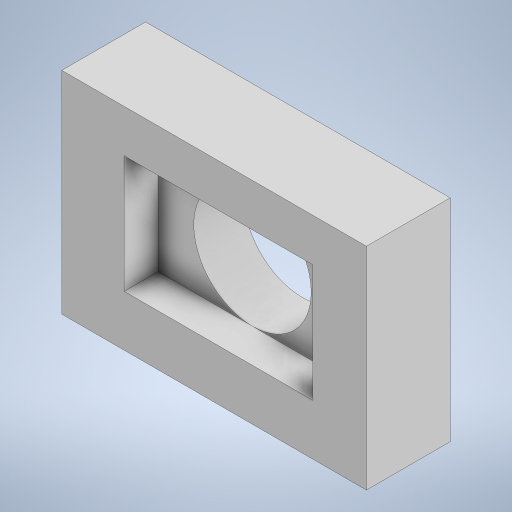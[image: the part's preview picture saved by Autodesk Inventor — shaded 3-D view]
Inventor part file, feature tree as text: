
AUTODESK INVENTOR PART (.ipt)
format: ipt  version: 2023 (Build 270158000, 158)  size: 631,296 bytes
history: native  units: in
note: dims shown in document units (in); Inventor stores cm internally (conversion verified against a paired STEP export)
features: extrude x18, sketch x16, fillet x2
ambient origin geometry x8: Origin, YZ Plane, XZ Plane, XY Plane, X Axis, Y Axis, Z Axis, Center Point
bodies: Solid1 (feature_tree)
feature tree (36):
  extrude  "Extrusion1"  Depth=4.5in
  extrude  "Extrusion2"  Depth=0.2in
  fillet  "Fillet1"  Radius=1.4in
  extrude  "Extrusion3"  Depth=0.25in
  extrude  "Extrusion4"  Depth=2.2875in
  extrude  "Extrusion5"  Depth=0.5437in
  sketch  "Sketch6"  dims[d13=0.75in d14=1.4in d15=0.0in]
  extrude  "Extrusion6"  Depth=1.4in TaperAngle=0.0deg
  extrude  "Extrusion9"  Depth=0.14in
  extrude  "Extrusion10"  Depth=0.275in
  extrude  "Extrusion11"  Depth=0.25in
  extrude  "Extrusion12"  Depth=0.15in
  extrude  "Extrusion13"  Depth=0.7in
  extrude  "Extrusion14"  Depth=0.1in
  extrude  "Extrusion15"  Depth=0.615in
  extrude  "Extrusion16"  Depth=1.1in
  fillet  "Fillet2"  Radius=0.21in
  extrude  "Extrusion17"  Depth=0.5575in
  extrude  "Extrusion18"  Depth=0.14in
  extrude  "Extrusion19"  Depth=0.14in
  extrude  "Extrusion20"  Depth=0.14in
  sketch  "Sketch1"  dims[d0=7.0in d1=4.5in]
  sketch  "Sketch2"  dims[d2=1.5in d3=0.0in d4=0.2in d5=1.4in d6=0.0in]
  sketch  "Sketch3"  dims[d7=0.125in d8=0.25in]
  sketch  "Sketch4"  dims[d9=0.25in d10=2.2875in]
  sketch  "Sketch5"  dims[d11=3.4125in d12=0.5437in]
  sketch  "Sketch8"  dims[d16=0.1in d17=0.14in]
  sketch  "Sketch9"  dims[d18=0.1in d19=0.275in]
  sketch  "Sketch10"  dims[d20=0.35in d21=0.25in]
  sketch  "Sketch11"  dims[d22=0.15in d23=0.15in]
  sketch  "Sketch12"  dims[d24=0.25in d25=0.7in]
  sketch  "Sketch13"  dims[d26=0.1in d27=0.1in]
  sketch  "Sketch14"  dims[d28=0.25in d29=0.615in]
  sketch  "Sketch15"  dims[d30=0.25in d31=1.1in d32=0.21in]
  sketch  "Sketch16"  dims[d33=0.3075in d34=0.5575in]
  sketch  "Sketch17"  dims[d35=1.65in d36=0.3075in d37=0.21in d38=0.5575in d39=2.1in d40=0.1in d41=0.1in d42=0.3in d43=0.1in d44=0.25in d45=0.615in d46=2.4in d47=0.11in d48=2.51in d49=0.5575in d50=0.1in d51=0.615in d52=0.175in d53=0.175in d54=0.1in d55=0.1in d56=0.25in d57=3.15in d58=0.1in d59=0.515in d60=0.05in d61=0.0in d62=0.1562in d63=0.1562in d64=0.2188in d65=0.2188in d66=0.2188in d67=0.2188in d68=0.2188in d69=0.2188in d70=0.625in d71=0.625in d72=0.625in d73=0.625in d74=0.8906in d76=2.25in d77=0.3in d78=0.3in d79=0.3in d80=0.3in d81=0.3in d82=0.625in d83=0.625in d84=0.625in d85=0.625in d86=1.0in d87=3.1in d88=3.1in d89=3.1in d90=3.1in d91=3.1in d92=1.0in d93=0.0in d97=0.4in d98=0.4in d99=0.4in d100=0.4in d101=0.4in d102=0.05in d103=0.0in d119=0.075in d120=0.075in d121=0.075in d122=0.075in d123=0.075in d124=0.0688in d125=0.0in d126=0.25in d127=0.275in d128=0.25in d129=0.25in d130=0.25in d131=2.1in d132=0.125in d133=0.0625in d134=0.05in d135=0.0in d136=0.6in d137=3.35in d139=0.3in d140=0.3155in d141=0.3157in d142=0.0375in d143=0.0in d144=2.0in d145=0.8125in d146=0.0825in d147=0.35in d148=0.15in d149=0.1in d150=0.7in d151=0.2in d152=0.0in d153=0.075in d154=0.125in d155=0.0in d156=0.28in d157=2.5in d158=0.49in d159=0.25in d160=0.0in d161=0.45in d162=0.081in d163=0.0in d164=0.45in d166=0.2in d167=0.2in d168=0.2in d169=0.075in d170=0.075in d171=0.075in d172=0.075in d173=0.2in d174=0.2in d175=0.2in d176=0.2in d177=0.075in d178=0.0in d179=0.125in d180=0.0375in d181=0.0375in d182=2.0in d183=0.5in d184=0.0in d185=0.0in d187=2.8in d188=5.0in d189=0.0in d190=5.0in d191=0.0in d192=1.0in d193=0.0in d194=0.28in d195=0.14in d196=0.14in d197=0.245in]
